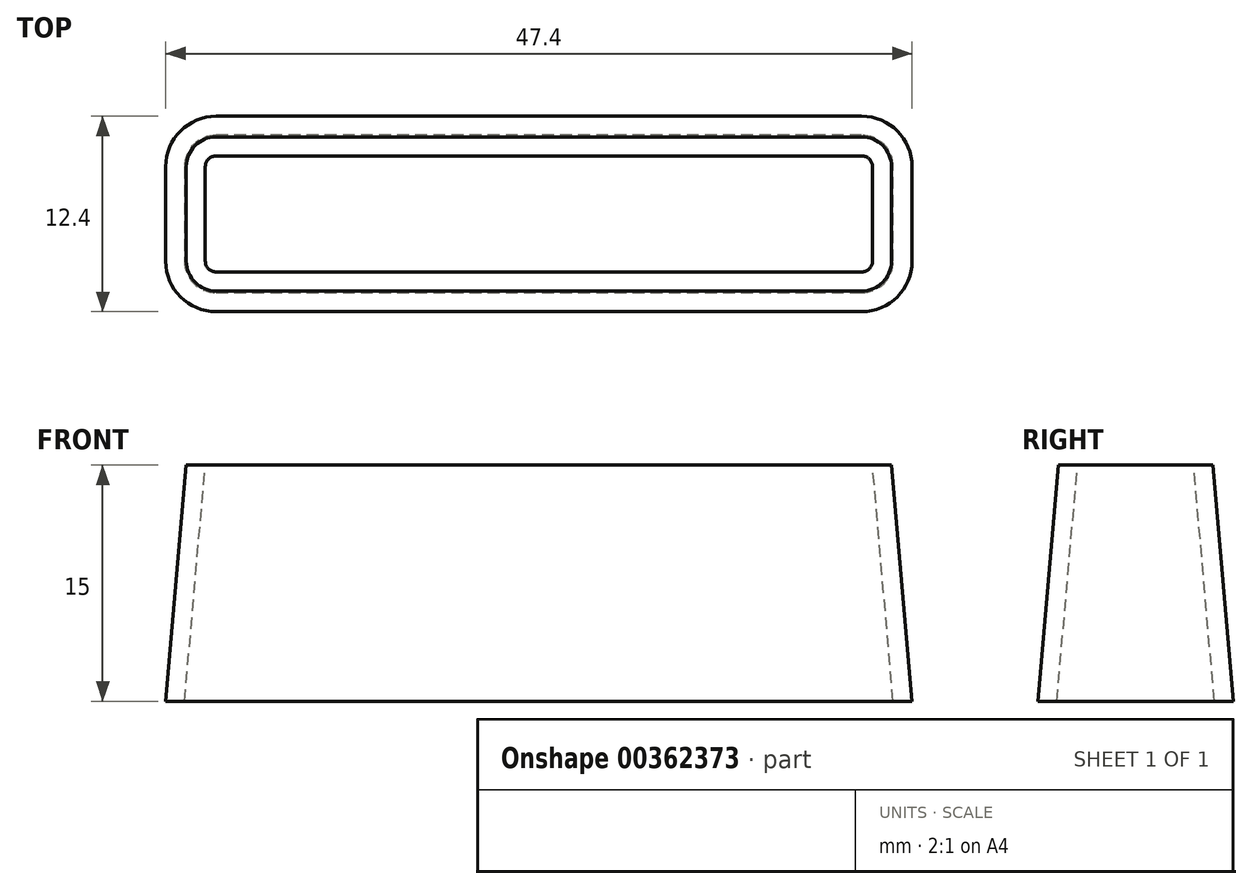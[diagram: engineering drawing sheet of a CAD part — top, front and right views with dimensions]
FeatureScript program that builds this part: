
annotation { "Feature Type Name" : "Feature", "Feature Type Description" : "" }
export const myFeature = defineFeature(function(context is Context, id is Id, definition is map)
    precondition{}
    {
        {
            var Q0;
            Q0=qCreatedBy(makeId("Top.planeOp"),FACE);
            var sketch = newSketch(context, id + "F0", { "sketchPlane" : qUnion([Q0])});
            skLineSegment(sketch, "E0.bottom", {"start": v(20.5, -5) * mm, "end": v(-20.5, -5) * mm});
            skLineSegment(sketch, "E0.top", {"start": v(20.5, 5) * mm, "end": v(-20.5, 5) * mm});
            skLineSegment(sketch, "E0.left", {"start": v(22.5, -3) * mm, "end": v(22.5, 3) * mm});
            skLineSegment(sketch, "E0.right", {"start": v(-22.5, -3) * mm, "end": v(-22.5, 3) * mm});
            skPoint(sketch, "E0.middle", {"position": v(0, 0) * mm});
            skPoint(sketch, "E1.visualSharp", {"position": v(-22.5, 5) * mm});
            skArc(sketch, "E1.filletArc", {"start": v(-20.5, 5) * mm, "mid": v(-21.91, 4.41) * mm, "end": v(-22.5, 3) * mm});
            skPoint(sketch, "E2.visualSharp", {"position": v(-22.5, -5) * mm});
            skArc(sketch, "E2.filletArc", {"start": v(-22.5, -3) * mm, "mid": v(-21.91, -4.41) * mm, "end": v(-20.5, -5) * mm});
            skPoint(sketch, "E3.visualSharp", {"position": v(22.5, -5) * mm});
            skArc(sketch, "E3.filletArc", {"start": v(20.5, -5) * mm, "mid": v(21.91, -4.41) * mm, "end": v(22.5, -3) * mm});
            skPoint(sketch, "E4.visualSharp", {"position": v(22.5, 5) * mm});
            skArc(sketch, "E4.filletArc", {"start": v(22.5, 3) * mm, "mid": v(21.91, 4.41) * mm, "end": v(20.5, 5) * mm});
            skSolve(sketch);
        }
        {
            var Q0;
            Q0=qCreatedBy(makeId("Front.planeOp"),FACE);
            var Q1;
            Q1=sQuery(id+"F0.wireOp",VERTEX,"E0.left.start");
            cPlane(context, id + "F1", {"entities" : qUnion([Q0, Q1]), "cplaneType" : CPlaneType.PLANE_POINT, "offset" : 25 * mm, "oppositeDirection" : true, "width" : 150 * mm, "height" : 150 * mm});
        }
        {
            var Q0;
            Q0=qCreatedBy(id+"F1.planeOp",FACE);
            var sketch = newSketch(context, id + "F2", { "sketchPlane" : qUnion([Q0])});
            skLineSegment(sketch, "E5", {"start": v(22.5, 0) * mm, "end": v(21.19, 15) * mm});
            skLineSegment(sketch, "E6", {"start": v(21.19, 15) * mm, "end": v(22.4, 15) * mm});
            skLineSegment(sketch, "E7", {"start": v(22.4, 15) * mm, "end": v(23.7, 0) * mm});
            skLineSegment(sketch, "E8", {"start": v(23.7, 0) * mm, "end": v(22.5, 0) * mm});
            skSolve(sketch);
        }
        {
            var Q0;
            Q0=makeQuery(id+"F2.imprint","IMPRINT",FACE,{"disambiguationData":[TD([[makeQuery(id+"F2.imprint","IMPRINT",EDGE,{"derivedFrom":sQuery(id+"F2.wireOp",EDGE,"E5")}),-1.0]])]});
            var Q1;
            Q1=sQuery(id+"F0.wireOp",EDGE,"E0.left");
            var Q2;
            Q2=sQuery(id+"F0.wireOp",EDGE,"E4.filletArc");
            var Q3;
            Q3=sQuery(id+"F0.wireOp",EDGE,"E0.top");
            var Q4;
            Q4=sQuery(id+"F0.wireOp",EDGE,"E1.filletArc");
            var Q5;
            Q5=sQuery(id+"F0.wireOp",EDGE,"E0.right");
            var Q6;
            Q6=sQuery(id+"F0.wireOp",EDGE,"E2.filletArc");
            var Q7;
            Q7=sQuery(id+"F0.wireOp",EDGE,"E0.bottom");
            var Q8;
            Q8=sQuery(id+"F0.wireOp",EDGE,"E3.filletArc");
            sweep(context, id + "F3", {"profiles" : qUnion([Q0]), "path" : qUnion([Q1, Q2, Q3, Q4, Q5, Q6, Q7, Q8])});
        }
    });
